# Revit family: Reece_Pipe Fitting_CTS_Flange Adaptor_Table-E
name_source: partatom
category: Pipe Fittings
revit_build: Autodesk Revit 2018 (Build: 20181011_1500(x64)
units: mm (PartAtom-declared; Revit-internal decimal feet)

## family parameters
Always vertical = No
Cut with Voids When Loaded = No
OmniClass Number = 23.60.30.11.14
OmniClass Title = Pipework Fittings
Part Type = Union
Round Connector Dimension = Use Diameter
Shared = Yes
Work Plane-Based = No

## types (1)
- Standard
    Description = 32 mm CTS Copper Companion Flange Table E
    Disclaimer = THIS FILE IS THE PROPERTY OF THE REECE GROUP. IT MAY NOT BE REPRODUCED, REVERSE-ENGINEERED, OR MODIFIED. ANY REPUBLICATION, TRANSMISSION, OR DISTRIBUTION FOR THE PURPOSE OF COMMERCIALLY EXPLOITING THE FILES IS PROHIBITED.
    K Coefficient Table = Tee
    Keynote = Product #1001598, Reece_Pipe Fitting_CTS_Flange Adaptor_Table-E - Standard
    Loss Method = Not Defined
    Manufacturer = CTS
    Reece_Detail_Disclaimer = THIS FILE IS THE PROPERTY OF THE REECE GROUP. IT MAY NOT BE REPRODUCED, REVERSE-ENGINEERED, OR MODIFIED. ANY REPUBLICATION, TRANSMISSION, OR DISTRIBUTION FOR THE PURPOSE OF COMMERCIALLY EXPLOITING THE FILES IS PROHIBITED.
    Reece_Lookup_Table = Reece_Pipe Fitting_CTS_Flange Adaptor_Table-E
    Reece_Material_Colour = Reece_Rubber_Black
    Reece_Material_Main = Reece_Metal_Copper
    Reece_Material_Secondary = Reece_Metal_Steel Enamelled_Blue
    Type Comments = Pipe Fitting

## geometry (parser evidence)
native form markers: Sweep x2
no freeform markers — native parametric forms only
